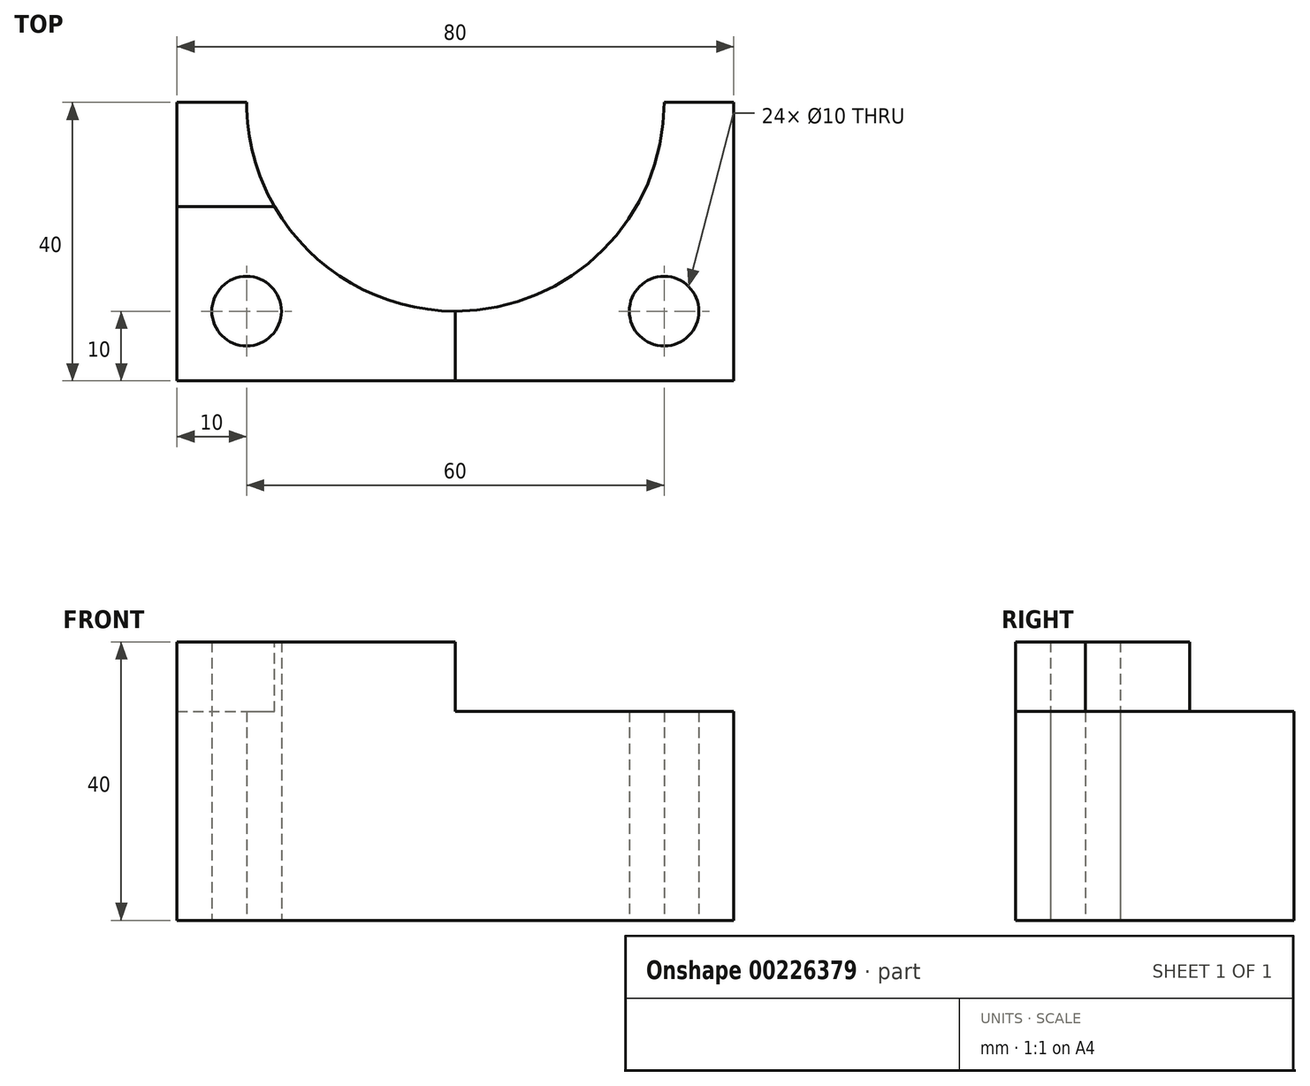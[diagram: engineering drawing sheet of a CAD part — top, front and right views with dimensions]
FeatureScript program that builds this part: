
annotation { "Feature Type Name" : "Feature", "Feature Type Description" : "" }
export const myFeature = defineFeature(function(context is Context, id is Id, definition is map)
    precondition{}
    {
        {
            var Q0;
            Q0=qCreatedBy(makeId("Top.planeOp"),FACE);
            var sketch = newSketch(context, id + "F0", { "sketchPlane" : qUnion([Q0])});
            skArc(sketch, "E0", {"start": v(-30, 0) * mm, "mid": v(0, -30) * mm, "end": v(30, 0) * mm});
            skLineSegment(sketch, "E1", {"start": v(-40, 0) * mm, "end": v(-40, -40) * mm});
            skLineSegment(sketch, "E2", {"start": v(-40, -40) * mm, "end": v(40, -40) * mm});
            skLineSegment(sketch, "E3", {"start": v(40, -40) * mm, "end": v(40, 0) * mm});
            skLineSegment(sketch, "E4", {"start": v(40, 0) * mm, "end": v(30, 0) * mm});
            skLineSegment(sketch, "E5", {"start": v(-40, 0) * mm, "end": v(-30, 0) * mm});
            skCircle(sketch, "E6", {"center": v(-30, -30) * mm, "radius": 5 * mm});
            skCircle(sketch, "E7", {"center": v(30, -30) * mm, "radius": 5 * mm});
            skSolve(sketch);
        }
        {
            var Q0;
            Q0=makeQuery(id+"F0.imprint","IMPRINT",FACE,{"disambiguationData":[TD([[makeQuery(id+"F0.imprint","IMPRINT",EDGE,{"derivedFrom":sQuery(id+"F0.wireOp",EDGE,"E0")}),-1.0]])]});
            extrude(context, id + "F1", {"entities" : qUnion([Q0]), "depth" : 40 * mm});
        }
        {
            var Q0;
            Q0=makeQuery(id+"F1.opExtrude","CAP_FACE",FACE,{"disambiguationData":[OSD([sQuery(id+"F0.wireOp",EDGE,"E0"),sQuery(id+"F0.wireOp",EDGE,"E1"),sQuery(id+"F0.wireOp",EDGE,"E2"),sQuery(id+"F0.wireOp",EDGE,"E3"),sQuery(id+"F0.wireOp",EDGE,"E4"),sQuery(id+"F0.wireOp",EDGE,"E5"),sQuery(id+"F0.wireOp",EDGE,"E6"),sQuery(id+"F0.wireOp",EDGE,"E7")])],"isStart":false});
            var sketch = newSketch(context, id + "F2", { "sketchPlane" : qUnion([Q0])});
            skLineSegment(sketch, "E8", {"start": v(-40, -15) * mm, "end": v(-25.98, -15) * mm});
            skLineSegment(sketch, "E9", {"start": v(0, -30) * mm, "end": v(0, -40) * mm});
            skSolve(sketch);
        }
        {
            var Q0;
            {var subQ0=sQuery(id+"F2.wireOp",EDGE,"E8");Q0=makeQuery(id+"F2.imprint","IMPRINT",FACE,{"disambiguationData":[TD([[makeQuery(id+"F2.imprint","IMPRINT",EDGE,{"derivedFrom":subQ0}),1.0]])]});}
            var Q1;
            {var subQ2=sQuery(id+"F2.wireOp",EDGE,"E9");Q1=makeQuery(id+"F2.imprint","IMPRINT",FACE,{"disambiguationData":[TD([[makeQuery(id+"F2.imprint","IMPRINT",EDGE,{"derivedFrom":subQ2}),1.0]])]});}
            extrude(context, id + "F3", {"entities" : qUnion([Q0, Q1]), "operationType" : NewBodyOperationType.REMOVE, "oppositeDirection" : true, "depth" : 10 * mm});
        }
    });
